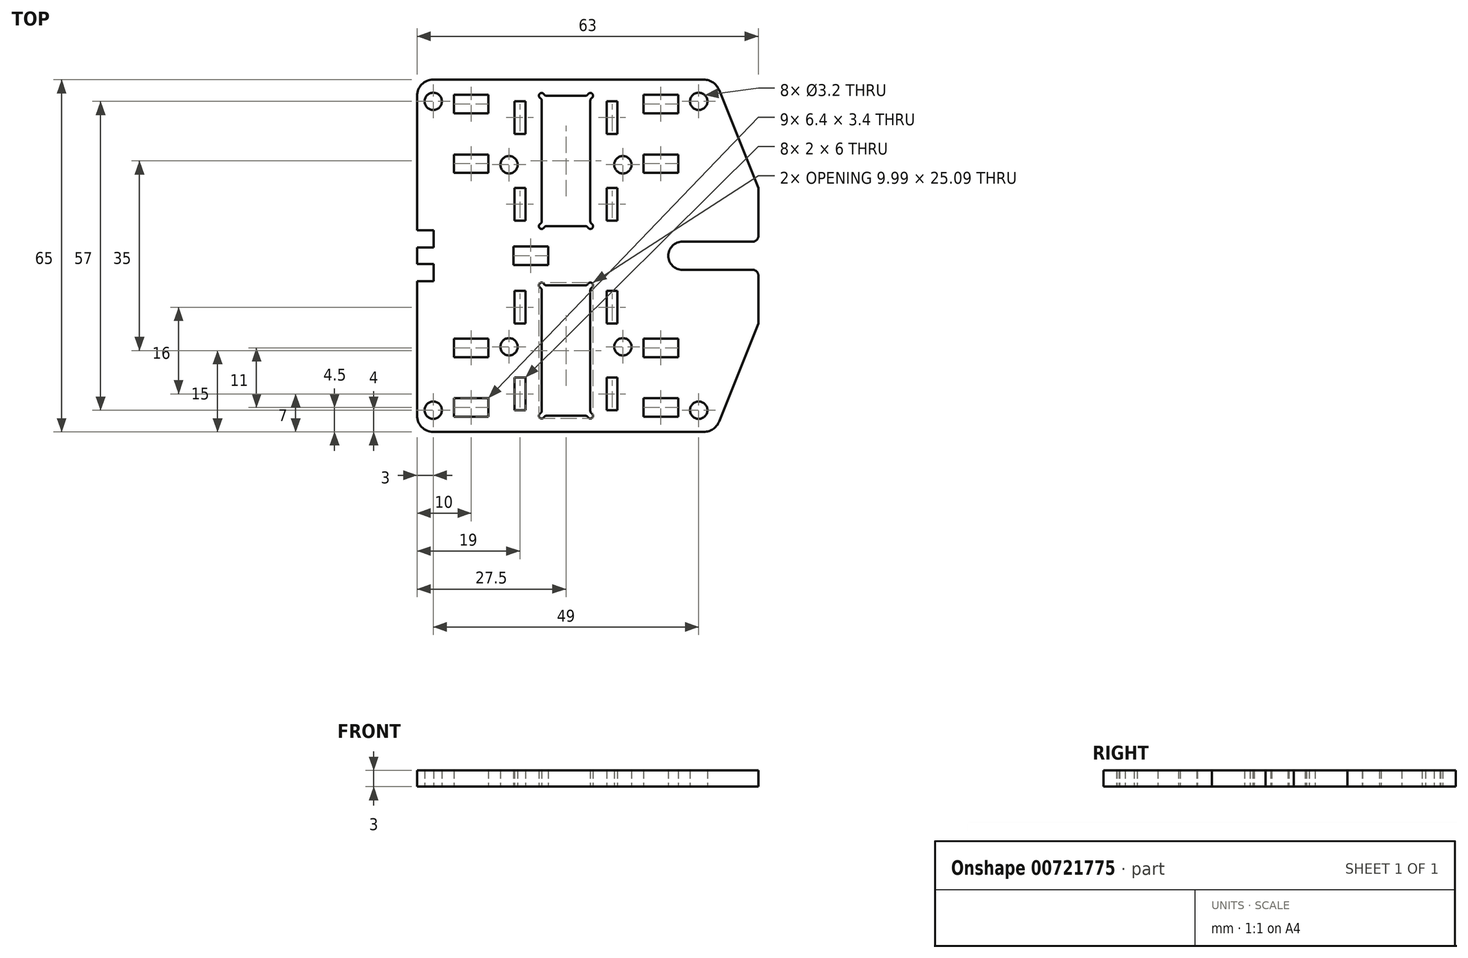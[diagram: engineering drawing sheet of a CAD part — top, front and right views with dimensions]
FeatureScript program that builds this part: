
annotation { "Feature Type Name" : "Feature", "Feature Type Description" : "" }
export const myFeature = defineFeature(function(context is Context, id is Id, definition is map)
    precondition{}
    {
        {
            var Q0;
            Q0=qCreatedBy(makeId("Top.planeOp"),FACE);
            var sketch = newSketch(context, id + "F0", { "sketchPlane" : qUnion([Q0])});
            skLineSegment(sketch, "E0", {"start": v(-31.5, -1.5) * mm, "end": v(-31.5, 1.5) * mm});
            skArc(sketch, "E1", {"start": v(-8.75, -29.12) * mm, "mid": v(-8.85, -29.9) * mm, "end": v(-8.07, -29.8) * mm});
            skArc(sketch, "E2", {"start": v(-7.63, -29.55) * mm, "mid": v(-7.88, -29.62) * mm, "end": v(-8.07, -29.8) * mm});
            skArc(sketch, "E3", {"start": v(-8.75, -29.12) * mm, "mid": v(-8.57, -28.93) * mm, "end": v(-8.5, -28.68) * mm});
            skLineSegment(sketch, "E4", {"start": v(-8.5, -6.32) * mm, "end": v(-8.5, -28.68) * mm});
            skArc(sketch, "E5", {"start": v(-8.5, -6.32) * mm, "mid": v(-8.57, -6.07) * mm, "end": v(-8.75, -5.88) * mm});
            skArc(sketch, "E6", {"start": v(-8.07, -5.2) * mm, "mid": v(-8.85, -5.1) * mm, "end": v(-8.75, -5.88) * mm});
            skArc(sketch, "E7", {"start": v(-8.07, -5.2) * mm, "mid": v(-7.88, -5.38) * mm, "end": v(-7.63, -5.45) * mm});
            skLineSegment(sketch, "E8", {"start": v(-0.37, -5.45) * mm, "end": v(-7.63, -5.45) * mm});
            skArc(sketch, "E9", {"start": v(-0.37, -5.45) * mm, "mid": v(-0.12, -5.38) * mm, "end": v(0.07, -5.2) * mm});
            skArc(sketch, "E10", {"start": v(0.75, -5.88) * mm, "mid": v(0.85, -5.1) * mm, "end": v(0.07, -5.2) * mm});
            skArc(sketch, "E11", {"start": v(0.75, -5.88) * mm, "mid": v(0.57, -6.07) * mm, "end": v(0.5, -6.32) * mm});
            skLineSegment(sketch, "E12", {"start": v(0.5, -28.68) * mm, "end": v(0.5, -6.32) * mm});
            skArc(sketch, "E13", {"start": v(0.5, -28.68) * mm, "mid": v(0.57, -28.93) * mm, "end": v(0.75, -29.12) * mm});
            skArc(sketch, "E14", {"start": v(0.07, -29.8) * mm, "mid": v(0.85, -29.9) * mm, "end": v(0.75, -29.12) * mm});
            skArc(sketch, "E15", {"start": v(0.07, -29.8) * mm, "mid": v(-0.12, -29.62) * mm, "end": v(-0.37, -29.55) * mm});
            skLineSegment(sketch, "E16", {"start": v(-7.63, -29.55) * mm, "end": v(-0.37, -29.55) * mm});
            skArc(sketch, "E17", {"start": v(-8.75, 5.88) * mm, "mid": v(-8.85, 5.1) * mm, "end": v(-8.07, 5.2) * mm});
            skArc(sketch, "E18", {"start": v(-7.63, 5.45) * mm, "mid": v(-7.88, 5.38) * mm, "end": v(-8.07, 5.2) * mm});
            skArc(sketch, "E19", {"start": v(-8.75, 5.88) * mm, "mid": v(-8.57, 6.07) * mm, "end": v(-8.5, 6.32) * mm});
            skLineSegment(sketch, "E20", {"start": v(-8.5, 28.68) * mm, "end": v(-8.5, 6.32) * mm});
            skArc(sketch, "E21", {"start": v(-8.5, 28.68) * mm, "mid": v(-8.57, 28.93) * mm, "end": v(-8.75, 29.12) * mm});
            skArc(sketch, "E22", {"start": v(-8.07, 29.8) * mm, "mid": v(-8.85, 29.9) * mm, "end": v(-8.75, 29.12) * mm});
            skArc(sketch, "E23", {"start": v(-8.07, 29.8) * mm, "mid": v(-7.88, 29.62) * mm, "end": v(-7.63, 29.55) * mm});
            skLineSegment(sketch, "E24", {"start": v(-0.37, 29.55) * mm, "end": v(-7.63, 29.55) * mm});
            skArc(sketch, "E25", {"start": v(-0.37, 29.55) * mm, "mid": v(-0.12, 29.62) * mm, "end": v(0.07, 29.8) * mm});
            skArc(sketch, "E26", {"start": v(0.75, 29.12) * mm, "mid": v(0.85, 29.9) * mm, "end": v(0.07, 29.8) * mm});
            skArc(sketch, "E27", {"start": v(0.75, 29.12) * mm, "mid": v(0.57, 28.93) * mm, "end": v(0.5, 28.68) * mm});
            skLineSegment(sketch, "E28", {"start": v(0.5, 6.32) * mm, "end": v(0.5, 28.68) * mm});
            skArc(sketch, "E29", {"start": v(0.5, 6.32) * mm, "mid": v(0.57, 6.07) * mm, "end": v(0.75, 5.88) * mm});
            skArc(sketch, "E30", {"start": v(0.07, 5.2) * mm, "mid": v(0.85, 5.1) * mm, "end": v(0.75, 5.88) * mm});
            skArc(sketch, "E31", {"start": v(0.07, 5.2) * mm, "mid": v(-0.12, 5.38) * mm, "end": v(-0.37, 5.45) * mm});
            skLineSegment(sketch, "E32", {"start": v(-7.63, 5.45) * mm, "end": v(-0.37, 5.45) * mm});
            skLineSegment(sketch, "E33", {"start": v(-31.5, -4.7) * mm, "end": v(-28.4, -4.7) * mm});
            skLineSegment(sketch, "E34", {"start": v(-28.4, -1.5) * mm, "end": v(-31.5, -1.5) * mm});
            skLineSegment(sketch, "E35", {"start": v(-28.4, -4.7) * mm, "end": v(-28.4, -1.5) * mm});
            skLineSegment(sketch, "E36", {"start": v(-31.5, 1.5) * mm, "end": v(-28.4, 1.5) * mm});
            skLineSegment(sketch, "E37", {"start": v(-28.4, 4.7) * mm, "end": v(-31.5, 4.7) * mm});
            skLineSegment(sketch, "E38", {"start": v(-28.4, 1.5) * mm, "end": v(-28.4, 4.7) * mm});
            skLineSegment(sketch, "E39", {"start": v(-13.7, 1.7) * mm, "end": v(-13.7, -1.7) * mm});
            skLineSegment(sketch, "E40", {"start": v(-13.7, -1.7) * mm, "end": v(-7.3, -1.7) * mm});
            skLineSegment(sketch, "E41", {"start": v(-13.7, 1.7) * mm, "end": v(-7.3, 1.7) * mm});
            skLineSegment(sketch, "E42", {"start": v(-7.3, -1.7) * mm, "end": v(-7.3, 1.7) * mm});
            skLineSegment(sketch, "E43", {"start": v(3.5, -12.5) * mm, "end": v(5.5, -12.5) * mm});
            skLineSegment(sketch, "E44", {"start": v(-13.5, -12.5) * mm, "end": v(-11.5, -12.5) * mm});
            skLineSegment(sketch, "E45", {"start": v(5.5, 12.5) * mm, "end": v(3.5, 12.5) * mm});
            skLineSegment(sketch, "E46", {"start": v(-11.5, 12.5) * mm, "end": v(-13.5, 12.5) * mm});
            skLineSegment(sketch, "E47", {"start": v(3.5, 22.5) * mm, "end": v(5.5, 22.5) * mm});
            skLineSegment(sketch, "E48", {"start": v(-13.5, 22.5) * mm, "end": v(-11.5, 22.5) * mm});
            skLineSegment(sketch, "E49", {"start": v(5.5, -22.5) * mm, "end": v(3.5, -22.5) * mm});
            skLineSegment(sketch, "E50", {"start": v(-11.5, -22.5) * mm, "end": v(-13.5, -22.5) * mm});
            skLineSegment(sketch, "E51", {"start": v(-13.5, -28.5) * mm, "end": v(-11.5, -28.5) * mm});
            skLineSegment(sketch, "E52", {"start": v(-11.5, -6.5) * mm, "end": v(-13.5, -6.5) * mm});
            skLineSegment(sketch, "E53", {"start": v(-13.5, 6.5) * mm, "end": v(-11.5, 6.5) * mm});
            skLineSegment(sketch, "E54", {"start": v(-11.5, 28.5) * mm, "end": v(-13.5, 28.5) * mm});
            skLineSegment(sketch, "E55", {"start": v(3.5, -28.5) * mm, "end": v(5.5, -28.5) * mm});
            skLineSegment(sketch, "E56", {"start": v(5.5, -6.5) * mm, "end": v(3.5, -6.5) * mm});
            skLineSegment(sketch, "E57", {"start": v(3.5, 6.5) * mm, "end": v(5.5, 6.5) * mm});
            skLineSegment(sketch, "E58", {"start": v(5.5, 28.5) * mm, "end": v(3.5, 28.5) * mm});
            skLineSegment(sketch, "E59", {"start": v(-13.5, -22.5) * mm, "end": v(-13.5, -28.5) * mm});
            skLineSegment(sketch, "E60", {"start": v(-11.5, -28.5) * mm, "end": v(-11.5, -22.5) * mm});
            skLineSegment(sketch, "E61", {"start": v(-13.5, -6.5) * mm, "end": v(-13.5, -12.5) * mm});
            skLineSegment(sketch, "E62", {"start": v(-11.5, -12.5) * mm, "end": v(-11.5, -6.5) * mm});
            skLineSegment(sketch, "E63", {"start": v(-13.5, 12.5) * mm, "end": v(-13.5, 6.5) * mm});
            skLineSegment(sketch, "E64", {"start": v(-11.5, 6.5) * mm, "end": v(-11.5, 12.5) * mm});
            skLineSegment(sketch, "E65", {"start": v(-13.5, 28.5) * mm, "end": v(-13.5, 22.5) * mm});
            skLineSegment(sketch, "E66", {"start": v(-11.5, 22.5) * mm, "end": v(-11.5, 28.5) * mm});
            skLineSegment(sketch, "E67", {"start": v(3.5, -22.5) * mm, "end": v(3.5, -28.5) * mm});
            skLineSegment(sketch, "E68", {"start": v(5.5, -28.5) * mm, "end": v(5.5, -22.5) * mm});
            skLineSegment(sketch, "E69", {"start": v(3.5, -6.5) * mm, "end": v(3.5, -12.5) * mm});
            skLineSegment(sketch, "E70", {"start": v(5.5, -12.5) * mm, "end": v(5.5, -6.5) * mm});
            skLineSegment(sketch, "E71", {"start": v(3.5, 12.5) * mm, "end": v(3.5, 6.5) * mm});
            skLineSegment(sketch, "E72", {"start": v(5.5, 6.5) * mm, "end": v(5.5, 12.5) * mm});
            skLineSegment(sketch, "E73", {"start": v(3.5, 28.5) * mm, "end": v(3.5, 22.5) * mm});
            skLineSegment(sketch, "E74", {"start": v(5.5, 22.5) * mm, "end": v(5.5, 28.5) * mm});
            skArc(sketch, "E75", {"start": v(17.5, 2.6) * mm, "mid": v(14.9, 0) * mm, "end": v(17.5, -2.6) * mm});
            skLineSegment(sketch, "E76", {"start": v(31.5, 12.5) * mm, "end": v(31.5, 3.6) * mm});
            skLineSegment(sketch, "E77", {"start": v(17.5, 2.6) * mm, "end": v(30.5, 2.6) * mm});
            skArc(sketch, "E78", {"start": v(30.5, 2.6) * mm, "mid": v(31.2, 2.9) * mm, "end": v(31.5, 3.6) * mm});
            skLineSegment(sketch, "E79", {"start": v(17.5, -2.6) * mm, "end": v(30.5, -2.6) * mm});
            skLineSegment(sketch, "E80", {"start": v(31.5, -12.5) * mm, "end": v(31.5, -3.6) * mm});
            skArc(sketch, "E81", {"start": v(31.5, -3.6) * mm, "mid": v(31.2, -2.9) * mm, "end": v(30.5, -2.6) * mm});
            skLineSegment(sketch, "E82", {"start": v(10.3, -26.3) * mm, "end": v(10.3, -29.7) * mm});
            skLineSegment(sketch, "E83", {"start": v(10.3, -29.7) * mm, "end": v(16.7, -29.7) * mm});
            skLineSegment(sketch, "E84", {"start": v(10.3, -26.3) * mm, "end": v(16.7, -26.3) * mm});
            skLineSegment(sketch, "E85", {"start": v(16.7, -29.7) * mm, "end": v(16.7, -26.3) * mm});
            skLineSegment(sketch, "E86", {"start": v(10.3, -15.3) * mm, "end": v(10.3, -18.7) * mm});
            skLineSegment(sketch, "E87", {"start": v(10.3, -18.7) * mm, "end": v(16.7, -18.7) * mm});
            skLineSegment(sketch, "E88", {"start": v(10.3, -15.3) * mm, "end": v(16.7, -15.3) * mm});
            skLineSegment(sketch, "E89", {"start": v(16.7, -18.7) * mm, "end": v(16.7, -15.3) * mm});
            skLineSegment(sketch, "E90", {"start": v(10.3, 18.7) * mm, "end": v(10.3, 15.3) * mm});
            skLineSegment(sketch, "E91", {"start": v(10.3, 15.3) * mm, "end": v(16.7, 15.3) * mm});
            skLineSegment(sketch, "E92", {"start": v(10.3, 18.7) * mm, "end": v(16.7, 18.7) * mm});
            skLineSegment(sketch, "E93", {"start": v(16.7, 15.3) * mm, "end": v(16.7, 18.7) * mm});
            skLineSegment(sketch, "E94", {"start": v(10.3, 29.7) * mm, "end": v(10.3, 26.3) * mm});
            skLineSegment(sketch, "E95", {"start": v(10.3, 26.3) * mm, "end": v(16.7, 26.3) * mm});
            skLineSegment(sketch, "E96", {"start": v(10.3, 29.7) * mm, "end": v(16.7, 29.7) * mm});
            skLineSegment(sketch, "E97", {"start": v(16.7, 26.3) * mm, "end": v(16.7, 29.7) * mm});
            skCircle(sketch, "E98", {"center": v(20.5, -28.5) * mm, "radius": 1.6 * mm});
            skCircle(sketch, "E99", {"center": v(20.5, 28.5) * mm, "radius": 1.6 * mm});
            skLineSegment(sketch, "E100", {"start": v(-24.7, -26.3) * mm, "end": v(-24.7, -29.7) * mm});
            skLineSegment(sketch, "E101", {"start": v(-24.7, -29.7) * mm, "end": v(-18.3, -29.7) * mm});
            skLineSegment(sketch, "E102", {"start": v(-24.7, -26.3) * mm, "end": v(-18.3, -26.3) * mm});
            skLineSegment(sketch, "E103", {"start": v(-18.3, -29.7) * mm, "end": v(-18.3, -26.3) * mm});
            skLineSegment(sketch, "E104", {"start": v(-24.7, -15.3) * mm, "end": v(-24.7, -18.7) * mm});
            skLineSegment(sketch, "E105", {"start": v(-24.7, -18.7) * mm, "end": v(-18.3, -18.7) * mm});
            skLineSegment(sketch, "E106", {"start": v(-24.7, -15.3) * mm, "end": v(-18.3, -15.3) * mm});
            skLineSegment(sketch, "E107", {"start": v(-18.3, -18.7) * mm, "end": v(-18.3, -15.3) * mm});
            skLineSegment(sketch, "E108", {"start": v(-24.7, 18.7) * mm, "end": v(-24.7, 15.3) * mm});
            skLineSegment(sketch, "E109", {"start": v(-24.7, 15.3) * mm, "end": v(-18.3, 15.3) * mm});
            skLineSegment(sketch, "E110", {"start": v(-24.7, 18.7) * mm, "end": v(-18.3, 18.7) * mm});
            skLineSegment(sketch, "E111", {"start": v(-18.3, 15.3) * mm, "end": v(-18.3, 18.7) * mm});
            skLineSegment(sketch, "E112", {"start": v(-24.7, 29.7) * mm, "end": v(-24.7, 26.3) * mm});
            skLineSegment(sketch, "E113", {"start": v(-24.7, 26.3) * mm, "end": v(-18.3, 26.3) * mm});
            skLineSegment(sketch, "E114", {"start": v(-24.7, 29.7) * mm, "end": v(-18.3, 29.7) * mm});
            skLineSegment(sketch, "E115", {"start": v(-18.3, 26.3) * mm, "end": v(-18.3, 29.7) * mm});
            skCircle(sketch, "E116", {"center": v(-28.5, -28.5) * mm, "radius": 1.6 * mm});
            skCircle(sketch, "E117", {"center": v(-28.5, 28.5) * mm, "radius": 1.6 * mm});
            skCircle(sketch, "E118", {"center": v(-14.5, -16.8) * mm, "radius": 1.6 * mm});
            skCircle(sketch, "E119", {"center": v(6.5, -16.8) * mm, "radius": 1.6 * mm});
            skCircle(sketch, "E120", {"center": v(6.5, 16.8) * mm, "radius": 1.6 * mm});
            skCircle(sketch, "E121", {"center": v(-14.5, 16.8) * mm, "radius": 1.6 * mm});
            skArc(sketch, "E122", {"start": v(24.25, 30.61) * mm, "mid": v(23.15, 31.98) * mm, "end": v(21.47, 32.5) * mm});
            skLineSegment(sketch, "E123", {"start": v(31.5, -12.5) * mm, "end": v(24.25, -30.61) * mm});
            skArc(sketch, "E124", {"start": v(21.47, -32.5) * mm, "mid": v(23.15, -31.98) * mm, "end": v(24.25, -30.61) * mm});
            skLineSegment(sketch, "E125", {"start": v(-31.5, -29.5) * mm, "end": v(-31.5, -4.7) * mm});
            skLineSegment(sketch, "E126", {"start": v(21.47, -32.5) * mm, "end": v(-28.5, -32.5) * mm});
            skArc(sketch, "E127", {"start": v(-31.5, -29.5) * mm, "mid": v(-30.62, -31.62) * mm, "end": v(-28.5, -32.5) * mm});
            skLineSegment(sketch, "E128", {"start": v(-31.5, 4.7) * mm, "end": v(-31.5, 29.5) * mm});
            skLineSegment(sketch, "E129", {"start": v(21.47, 32.5) * mm, "end": v(-28.5, 32.5) * mm});
            skArc(sketch, "E130", {"start": v(-28.5, 32.5) * mm, "mid": v(-30.62, 31.62) * mm, "end": v(-31.5, 29.5) * mm});
            skLineSegment(sketch, "E131", {"start": v(24.25, 30.61) * mm, "end": v(31.5, 12.5) * mm});
            skSolve(sketch);
        }
        {
            var Q0;
            Q0=qSketchRegion(id+"F0",true);
            extrude(context, id + "F1", {"entities" : qUnion([Q0]), "depth" : 3 * mm, "offsetDistance" : 25 * mm});
        }
    });
